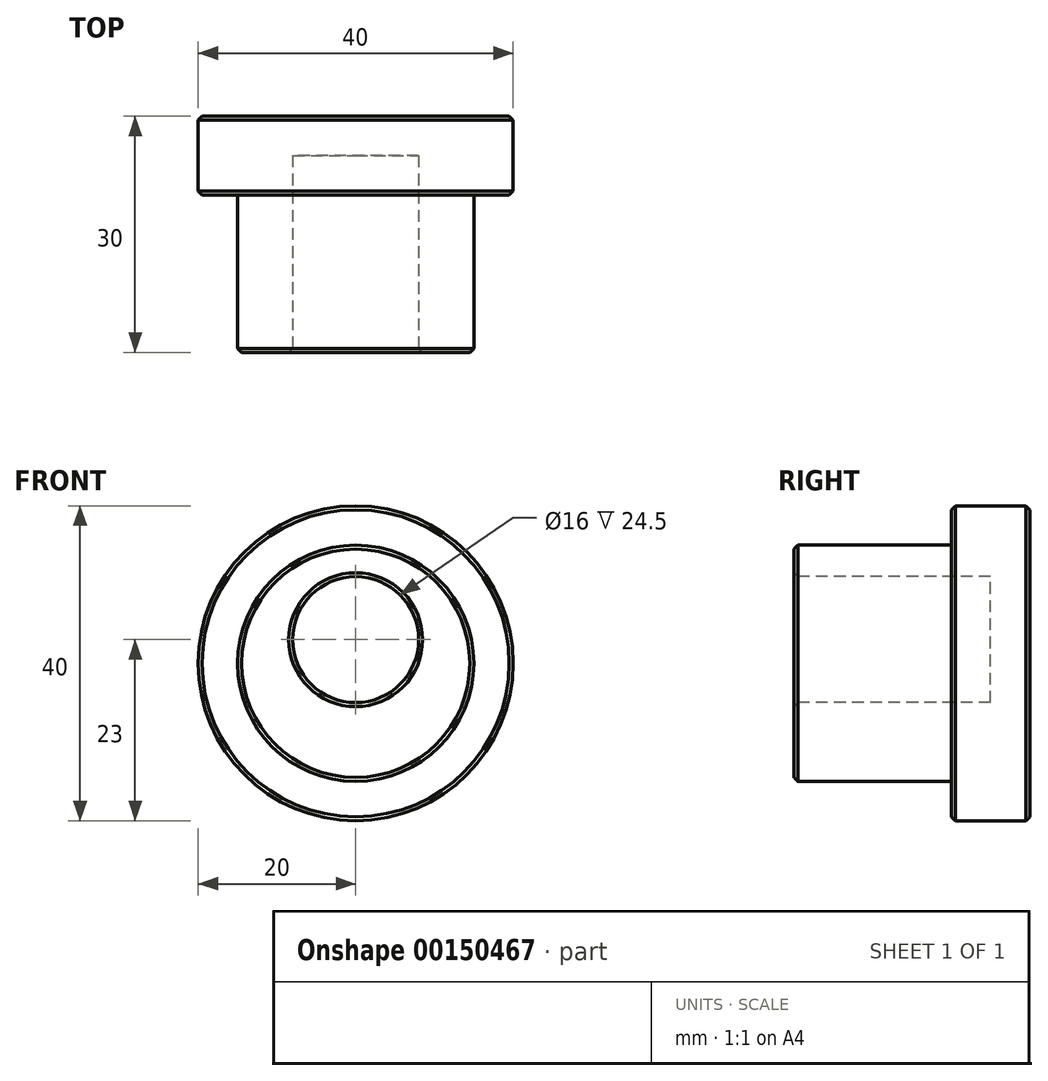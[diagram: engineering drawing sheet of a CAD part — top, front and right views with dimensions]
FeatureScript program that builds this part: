
annotation { "Feature Type Name" : "Feature", "Feature Type Description" : "" }
export const myFeature = defineFeature(function(context is Context, id is Id, definition is map)
    precondition{}
    {
        {
            var Q0;
            Q0=qCreatedBy(makeId("Front.planeOp"),FACE);
            var sketch = newSketch(context, id + "F0", { "sketchPlane" : qUnion([Q0])});
            skCircle(sketch, "E0", {"center": v(0, 0) * mm, "radius": 20 * mm});
            skSolve(sketch);
        }
        {
            var Q0;
            Q0=makeQuery(id+"F0.imprint","IMPRINT",FACE,{"disambiguationData":[TD([[makeQuery(id+"F0.imprint","IMPRINT",EDGE,{"derivedFrom":sQuery(id+"F0.wireOp",EDGE,"E0")}),1.0]])]});
            extrude(context, id + "F1", {"entities" : qUnion([Q0]), "depth" : 10 * mm});
        }
        {
            var Q0;
            Q0=makeQuery(id+"F1.opExtrude","CAP_FACE",FACE,{"disambiguationData":[OSD([sQuery(id+"F0.wireOp",EDGE,"E0")])],"isStart":false});
            var sketch = newSketch(context, id + "F2", { "sketchPlane" : qUnion([Q0])});
            skCircle(sketch, "E1", {"center": v(0, 0) * mm, "radius": 15 * mm});
            skSolve(sketch);
        }
        {
            var Q0;
            Q0=makeQuery(id+"F2.imprint","IMPRINT",FACE,{"disambiguationData":[TD([[makeQuery(id+"F2.imprint","IMPRINT",EDGE,{"derivedFrom":sQuery(id+"F2.wireOp",EDGE,"E1")}),1.0]])]});
            extrude(context, id + "F3", {"entities" : qUnion([Q0]), "operationType" : NewBodyOperationType.ADD, "depth" : 20 * mm});
        }
        {
            var Q0;
            Q0=makeQuery(id+"F3.opExtrude","CAP_FACE",FACE,{"disambiguationData":[OSD([sQuery(id+"F2.wireOp",EDGE,"E1")])],"isStart":false});
            var sketch = newSketch(context, id + "F4", { "sketchPlane" : qUnion([Q0])});
            skCircle(sketch, "E2", {"center": v(0, 3) * mm, "radius": 8 * mm});
            skSolve(sketch);
        }
        {
            var Q0;
            Q0 = qSketchRegion(id + "F4", true);
            extrude(context, id + "F5", {"entities" : qUnion([Q0]), "operationType" : NewBodyOperationType.REMOVE, "oppositeDirection" : true, "depth" : 25 * mm});
        }
        {
            var Q0;
            Q0=makeQuery(id+"F3.opExtrude","CAP_EDGE",EDGE,{"disambiguationData":[OSD([sQuery(id+"F2.wireOp",EDGE,"E1")])],"isStart":false});
            var Q1;
            Q1=makeQuery(id+"F1.opExtrude","CAP_EDGE",EDGE,{"disambiguationData":[OSD([sQuery(id+"F0.wireOp",EDGE,"E0")])],"isStart":false});
            var Q2;
            Q2=makeQuery(id+"F1.opExtrude","CAP_EDGE",EDGE,{"disambiguationData":[OSD([sQuery(id+"F0.wireOp",EDGE,"E0")])],"isStart":true});
            var Q3;
            Q3=makeQuery(id+"F5.boolean.opBoolean","INTERSECT",EDGE,{"derivedFrom":[makeQuery(id+"F3.opExtrude","CAP_FACE",FACE,{"disambiguationData":[OSD([sQuery(id+"F2.wireOp",EDGE,"E1")])],"isStart":false}),makeQuery(id+"F5.opExtrude","SWEPT_FACE",FACE,{"disambiguationData":[OSD([sQuery(id+"F4.wireOp",EDGE,"E2")])]})]});
            var Q4;
            Q4=makeQuery(id+"F5.boolean.opBoolean","COPY",EDGE,{"derivedFrom":makeQuery(id+"F5.opExtrude","CAP_EDGE",EDGE,{"disambiguationData":[OSD([sQuery(id+"F4.wireOp",EDGE,"E2")])],"isStart":true})});
            chamfer(context, id + "F6", {"entities" : qUnion([Q0, Q1, Q2, Q3, Q4]), "width" : 0.5 * mm, "tangentPropagation" : true});
        }
    });
